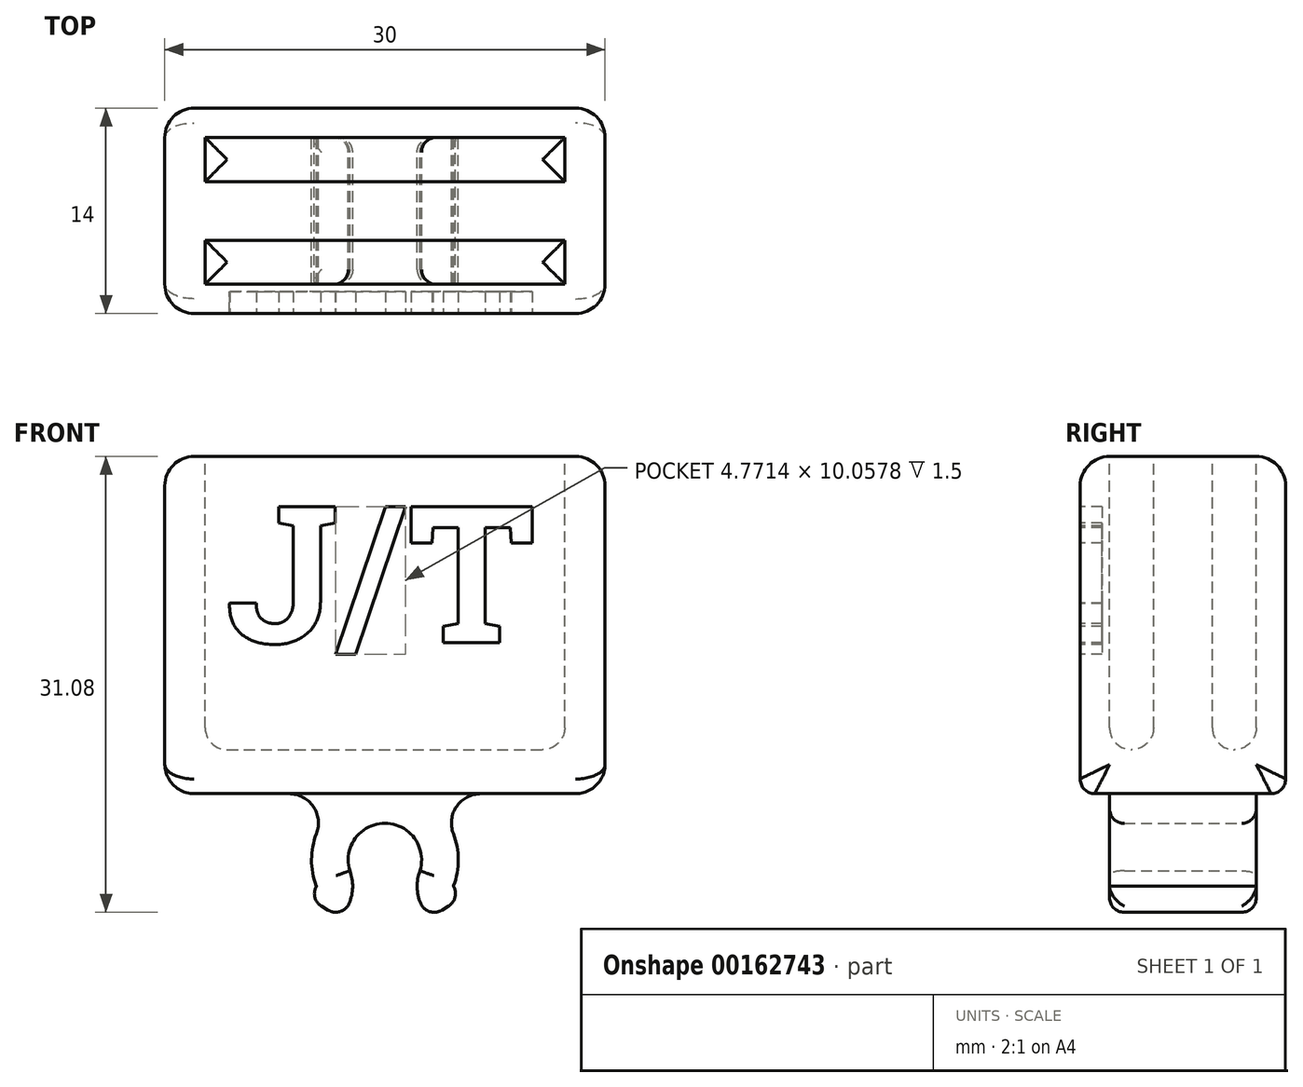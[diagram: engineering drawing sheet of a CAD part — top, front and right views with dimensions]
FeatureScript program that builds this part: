
annotation { "Feature Type Name" : "Feature", "Feature Type Description" : "" }
export const myFeature = defineFeature(function(context is Context, id is Id, definition is map)
    precondition{}
    {
        {
            var Q0;
            Q0=qCreatedBy(makeId("Front.planeOp"),FACE);
            var sketch = newSketch(context, id + "F0", { "sketchPlane" : qUnion([Q0])});
            skArc(sketch, "E0", {"start": v(2.39, -1.95) * mm, "mid": v(2.01, 0.27) * mm, "end": v(0, 1.28) * mm});
            skArc(sketch, "E1", {"start": v(2.39, -1.95) * mm, "mid": v(2.27, -3.64) * mm, "end": v(3.08, -5.12) * mm});
            skLineSegment(sketch, "E2", {"start": v(3.08, -5.12) * mm, "end": v(5.18, -3.84) * mm});
            skLineSegment(sketch, "E3", {"start": v(5.18, -3.84) * mm, "end": v(4.67, -3) * mm});
            skArc(sketch, "E4", {"start": v(4.67, -3) * mm, "mid": v(4.64, 0.64) * mm, "end": v(2.14, 3.3) * mm});
            skLineSegment(sketch, "E5", {"start": v(0, 8.47) * mm, "end": v(0, -7.46) * mm, "construction": true});
            skLineSegment(sketch, "E6", {"start": v(2.14, 3.3) * mm, "end": v(15, 3.3) * mm});
            skLineSegment(sketch, "E7", {"start": v(15, 3.3) * mm, "end": v(15, 26.3) * mm});
            skLineSegment(sketch, "E8", {"start": v(15, 26.3) * mm, "end": v(0, 26.3) * mm});
            skPoint(sketch, "E9.orphan", {"position": v(0, 3.78) * mm});
            skLineSegment(sketch, "E10.MirrorCS", {"start": v(-3.08, -5.12) * mm, "end": v(-5.18, -3.84) * mm});
            skLineSegment(sketch, "E11.MirrorCS", {"start": v(-5.18, -3.84) * mm, "end": v(-4.67, -3) * mm});
            skArc(sketch, "E12.MirrorCS", {"start": v(-2.39, -1.95) * mm, "mid": v(-2.27, -3.64) * mm, "end": v(-3.08, -5.12) * mm});
            skArc(sketch, "E13.MirrorCS", {"start": v(-2.39, -1.95) * mm, "mid": v(-2.01, 0.27) * mm, "end": v(0, 1.28) * mm});
            skLineSegment(sketch, "E14.MirrorCS", {"start": v(-15, 3.3) * mm, "end": v(-15, 26.3) * mm});
            skLineSegment(sketch, "E15.MirrorCS", {"start": v(-2.14, 3.3) * mm, "end": v(-15, 3.3) * mm});
            skLineSegment(sketch, "E16.MirrorCS", {"start": v(-15, 26.3) * mm, "end": v(0, 26.3) * mm});
            skArc(sketch, "E17.MirrorCS", {"start": v(-4.67, -3) * mm, "mid": v(-4.64, 0.64) * mm, "end": v(-2.14, 3.3) * mm});
            skSolve(sketch);
        }
        {
            var Q0;
            Q0=makeQuery(id+"F0.imprint","IMPRINT",FACE,{"disambiguationData":[TD([[makeQuery(id+"F0.imprint","IMPRINT",EDGE,{"derivedFrom":sQuery(id+"F0.wireOp",EDGE,"E0")}),-1.0]])]});
            extrude(context, id + "F1", {"entities" : qUnion([Q0]), "depth" : 10 * mm});
        }
        {
            var Q0;
            Q0=makeQuery(id+"F1.opExtrude","CAP_FACE",FACE,{"disambiguationData":[OSD([sQuery(id+"F0.wireOp",EDGE,"E0"),sQuery(id+"F0.wireOp",EDGE,"E1"),sQuery(id+"F0.wireOp",EDGE,"E2"),sQuery(id+"F0.wireOp",EDGE,"E3"),sQuery(id+"F0.wireOp",EDGE,"E4"),sQuery(id+"F0.wireOp",EDGE,"E6"),sQuery(id+"F0.wireOp",EDGE,"E7"),sQuery(id+"F0.wireOp",EDGE,"E8"),sQuery(id+"F0.wireOp",EDGE,"E10.MirrorCS"),sQuery(id+"F0.wireOp",EDGE,"E11.MirrorCS"),sQuery(id+"F0.wireOp",EDGE,"E12.MirrorCS"),sQuery(id+"F0.wireOp",EDGE,"E13.MirrorCS"),sQuery(id+"F0.wireOp",EDGE,"E14.MirrorCS"),sQuery(id+"F0.wireOp",EDGE,"E15.MirrorCS"),sQuery(id+"F0.wireOp",EDGE,"E16.MirrorCS"),sQuery(id+"F0.wireOp",EDGE,"E17.MirrorCS")])],"isStart":false});
            var sketch = newSketch(context, id + "F2", { "sketchPlane" : qUnion([Q0])});
            skLineSegment(sketch, "E18.bottom", {"start": v(-15, 3.3) * mm, "end": v(15, 3.3) * mm});
            skLineSegment(sketch, "E18.top", {"start": v(-15, 26.3) * mm, "end": v(15, 26.3) * mm});
            skLineSegment(sketch, "E18.left", {"start": v(-15, 3.3) * mm, "end": v(-15, 26.3) * mm});
            skLineSegment(sketch, "E18.right", {"start": v(15, 3.3) * mm, "end": v(15, 26.3) * mm});
            skSolve(sketch);
        }
        {
            var Q0;
            Q0 = qSketchRegion(id + "F2", true);
            extrude(context, id + "F3", {"entities" : qUnion([Q0]), "operationType" : NewBodyOperationType.ADD, "depth" : 2 * mm});
        }
        {
            var Q0;
            Q0=makeQuery(id+"F1.opExtrude","CAP_FACE",FACE,{"disambiguationData":[OSD([sQuery(id+"F0.wireOp",EDGE,"E0"),sQuery(id+"F0.wireOp",EDGE,"E1"),sQuery(id+"F0.wireOp",EDGE,"E2"),sQuery(id+"F0.wireOp",EDGE,"E3"),sQuery(id+"F0.wireOp",EDGE,"E4"),sQuery(id+"F0.wireOp",EDGE,"E6"),sQuery(id+"F0.wireOp",EDGE,"E7"),sQuery(id+"F0.wireOp",EDGE,"E8"),sQuery(id+"F0.wireOp",EDGE,"E10.MirrorCS"),sQuery(id+"F0.wireOp",EDGE,"E11.MirrorCS"),sQuery(id+"F0.wireOp",EDGE,"E12.MirrorCS"),sQuery(id+"F0.wireOp",EDGE,"E13.MirrorCS"),sQuery(id+"F0.wireOp",EDGE,"E14.MirrorCS"),sQuery(id+"F0.wireOp",EDGE,"E15.MirrorCS"),sQuery(id+"F0.wireOp",EDGE,"E16.MirrorCS"),sQuery(id+"F0.wireOp",EDGE,"E17.MirrorCS")])],"isStart":true});
            var sketch = newSketch(context, id + "F4", { "sketchPlane" : qUnion([Q0])});
            skLineSegment(sketch, "E19.bottom", {"start": v(-15, 3.3) * mm, "end": v(15, 3.3) * mm});
            skLineSegment(sketch, "E19.top", {"start": v(-15, 26.3) * mm, "end": v(15, 26.3) * mm});
            skLineSegment(sketch, "E19.left", {"start": v(-15, 3.3) * mm, "end": v(-15, 26.3) * mm});
            skLineSegment(sketch, "E19.right", {"start": v(15, 3.3) * mm, "end": v(15, 26.3) * mm});
            skSolve(sketch);
        }
        {
            var Q0;
            Q0 = qSketchRegion(id + "F4", true);
            extrude(context, id + "F5", {"entities" : qUnion([Q0]), "operationType" : NewBodyOperationType.ADD, "depth" : 2 * mm});
        }
        {
            var Q0;
            Q0=makeQuery(id+"F5.boolean.opBoolean","MERGE",FACE,{"derivedFrom":[makeQuery(id+"F3.boolean.opBoolean","MERGE",FACE,{"derivedFrom":[makeQuery(id+"F1.opExtrude","SWEPT_FACE",FACE,{"disambiguationData":[OSD([sQuery(id+"F0.wireOp",EDGE,"E8"),sQuery(id+"F0.wireOp",EDGE,"E16.MirrorCS")])]}),makeQuery(id+"F3.opExtrude","SWEPT_FACE",FACE,{"disambiguationData":[OSD([sQuery(id+"F2.wireOp",EDGE,"E18.top")])]})]}),makeQuery(id+"F5.opExtrude","SWEPT_FACE",FACE,{"disambiguationData":[OSD([sQuery(id+"F4.wireOp",EDGE,"E19.top")])]})]});
            var sketch = newSketch(context, id + "F6", { "sketchPlane" : qUnion([Q0])});
            skLineSegment(sketch, "E20.bottom", {"start": v(12.25, -10) * mm, "end": v(-12.25, -10) * mm});
            skLineSegment(sketch, "E20.top", {"start": v(12.25, -7) * mm, "end": v(-12.25, -7) * mm});
            skLineSegment(sketch, "E20.left", {"start": v(12.25, -10) * mm, "end": v(12.25, -7) * mm});
            skLineSegment(sketch, "E20.right", {"start": v(-12.25, -10) * mm, "end": v(-12.25, -7) * mm});
            skPoint(sketch, "E20.middle", {"position": v(0, -8.5) * mm});
            skLineSegment(sketch, "E21.bottom", {"start": v(12.25, -3) * mm, "end": v(-12.25, -3) * mm});
            skLineSegment(sketch, "E21.top", {"start": v(12.25, 0) * mm, "end": v(-12.25, 0) * mm});
            skLineSegment(sketch, "E21.left", {"start": v(12.25, -3) * mm, "end": v(12.25, 0) * mm});
            skLineSegment(sketch, "E21.right", {"start": v(-12.25, -3) * mm, "end": v(-12.25, 0) * mm});
            skPoint(sketch, "E21.middle", {"position": v(0, -1.5) * mm});
            skSolve(sketch);
        }
        {
            var Q0;
            Q0=makeQuery(id+"F6.imprint","IMPRINT",FACE,{"disambiguationData":[TD([[makeQuery(id+"F6.imprint","IMPRINT",EDGE,{"derivedFrom":sQuery(id+"F6.wireOp",EDGE,"E21.bottom")}),-1.0]])]});
            var Q1;
            Q1=makeQuery(id+"F6.imprint","IMPRINT",FACE,{"disambiguationData":[TD([[makeQuery(id+"F6.imprint","IMPRINT",EDGE,{"derivedFrom":sQuery(id+"F6.wireOp",EDGE,"E20.bottom")}),-1.0]])]});
            extrude(context, id + "F7", {"entities" : qUnion([Q0, Q1]), "operationType" : NewBodyOperationType.REMOVE, "oppositeDirection" : true, "depth" : 20 * mm});
        }
        {
            var Q0;
            Q0=makeQuery(id+"F3.opExtrude","CAP_FACE",FACE,{"disambiguationData":[OSD([sQuery(id+"F2.wireOp",EDGE,"E18.bottom"),sQuery(id+"F2.wireOp",EDGE,"E18.top"),sQuery(id+"F2.wireOp",EDGE,"E18.left"),sQuery(id+"F2.wireOp",EDGE,"E18.right")])],"isStart":false});
            var sketch = newSketch(context, id + "F8", { "sketchPlane" : qUnion([Q0])});
            skText(sketch, "E22", { "text": "J/T", "fontName": "RobotoSlab-Bold.ttf"});
            const initialGuessF8  = {"E22": [-0.01081, 0.01361, 1, 0, 0.00938]};
            skSetInitialGuess(sketch, initialGuessF8);
            skSolve(sketch);
        }
        {
            var Q0;
            Q0 = qSketchRegion(id + "F8", true);
            extrude(context, id + "F9", {"entities" : qUnion([Q0]), "operationType" : NewBodyOperationType.REMOVE, "oppositeDirection" : true, "depth" : 1.5 * mm});
        }
        {
            var Q0;
            Q0=makeQuery(id+"F1.opExtrude","SWEPT_FACE",FACE,{"disambiguationData":[OSD([sQuery(id+"F0.wireOp",EDGE,"E2")])]});
            var Q1;
            Q1=makeQuery(id+"F1.opExtrude","SWEPT_FACE",FACE,{"disambiguationData":[OSD([sQuery(id+"F0.wireOp",EDGE,"E10.MirrorCS")])]});
            var Q2;
            Q2=makeQuery(id+"F1.opExtrude","CAP_EDGE",EDGE,{"disambiguationData":[OSD([sQuery(id+"F0.wireOp",EDGE,"E1")])],"isStart":true});
            var Q3;
            Q3=makeQuery(id+"F1.opExtrude","CAP_EDGE",EDGE,{"disambiguationData":[OSD([sQuery(id+"F0.wireOp",EDGE,"E12.MirrorCS")])],"isStart":true});
            var Q4;
            Q4=makeQuery(id+"F1.opExtrude","CAP_EDGE",EDGE,{"disambiguationData":[OSD([sQuery(id+"F0.wireOp",EDGE,"E0"),sQuery(id+"F0.wireOp",EDGE,"E13.MirrorCS")])],"isStart":false});
            var Q5;
            Q5=makeQuery(id+"F1.opExtrude","CAP_EDGE",EDGE,{"disambiguationData":[OSD([sQuery(id+"F0.wireOp",EDGE,"E12.MirrorCS")])],"isStart":false});
            var Q6;
            Q6=makeQuery(id+"F1.opExtrude","CAP_EDGE",EDGE,{"disambiguationData":[OSD([sQuery(id+"F0.wireOp",EDGE,"E1")])],"isStart":false});
            fillet(context, id + "F10", {"entities" : qUnion([Q0, Q1, Q2, Q3, Q4, Q5, Q6]), "radius" : 1 * mm, "tangentPropagation" : true, "allowEdgeOverflow" : false});
        }
        {
            var Q0;
            Q0=makeQuery(id+"F1.opExtrude","SWEPT_EDGE",EDGE,{"disambiguationData":[OSD([sQuery(id+"F0.wireOp",EDGE,"E4"),sQuery(id+"F0.wireOp",EDGE,"E6")])]});
            var Q1;
            Q1=makeQuery(id+"F1.opExtrude","SWEPT_EDGE",EDGE,{"disambiguationData":[OSD([sQuery(id+"F0.wireOp",EDGE,"E15.MirrorCS"),sQuery(id+"F0.wireOp",EDGE,"E17.MirrorCS")])]});
            fillet(context, id + "F11", {"entities" : qUnion([Q0, Q1]), "radius" : 2 * mm, "tangentPropagation" : true, "allowEdgeOverflow" : false});
        }
        {
            var Q0;
            Q0=makeQuery(id+"F5.opExtrude","CAP_EDGE",EDGE,{"disambiguationData":[OSD([sQuery(id+"F4.wireOp",EDGE,"E19.left")])],"isStart":false});
            var Q1;
            Q1=makeQuery(id+"F5.opExtrude","CAP_EDGE",EDGE,{"disambiguationData":[OSD([sQuery(id+"F4.wireOp",EDGE,"E19.right")])],"isStart":false});
            var Q2;
            Q2=makeQuery(id+"F5.opExtrude","CAP_EDGE",EDGE,{"disambiguationData":[OSD([sQuery(id+"F4.wireOp",EDGE,"E19.top")])],"isStart":false});
            var Q3;
            Q3=makeQuery(id+"F5.boolean.opBoolean","MERGE",EDGE,{"derivedFrom":[makeQuery(id+"F3.boolean.opBoolean","MERGE",EDGE,{"derivedFrom":[makeQuery(id+"F1.opExtrude","SWEPT_EDGE",EDGE,{"disambiguationData":[OSD([sQuery(id+"F0.wireOp",EDGE,"E14.MirrorCS"),sQuery(id+"F0.wireOp",EDGE,"E16.MirrorCS")])]}),makeQuery(id+"F3.opExtrude","SWEPT_EDGE",EDGE,{"disambiguationData":[OSD([sQuery(id+"F2.wireOp",EDGE,"E18.top"),sQuery(id+"F2.wireOp",EDGE,"E18.left")])]})]}),makeQuery(id+"F5.opExtrude","SWEPT_EDGE",EDGE,{"disambiguationData":[OSD([sQuery(id+"F4.wireOp",EDGE,"E19.top"),sQuery(id+"F4.wireOp",EDGE,"E19.right")])]})]});
            var Q4;
            Q4=makeQuery(id+"F5.boolean.opBoolean","MERGE",FACE,{"derivedFrom":[makeQuery(id+"F3.boolean.opBoolean","MERGE",FACE,{"derivedFrom":[makeQuery(id+"F1.opExtrude","SWEPT_FACE",FACE,{"disambiguationData":[OSD([sQuery(id+"F0.wireOp",EDGE,"E14.MirrorCS")])]}),makeQuery(id+"F3.opExtrude","SWEPT_FACE",FACE,{"disambiguationData":[OSD([sQuery(id+"F2.wireOp",EDGE,"E18.left")])]})]}),makeQuery(id+"F5.opExtrude","SWEPT_FACE",FACE,{"disambiguationData":[OSD([sQuery(id+"F4.wireOp",EDGE,"E19.right")])]})]});
            var Q5;
            Q5=makeQuery(id+"F5.boolean.opBoolean","MERGE",FACE,{"derivedFrom":[makeQuery(id+"F3.boolean.opBoolean","MERGE",FACE,{"derivedFrom":[makeQuery(id+"F1.opExtrude","SWEPT_FACE",FACE,{"disambiguationData":[OSD([sQuery(id+"F0.wireOp",EDGE,"E7")])]}),makeQuery(id+"F3.opExtrude","SWEPT_FACE",FACE,{"disambiguationData":[OSD([sQuery(id+"F2.wireOp",EDGE,"E18.right")])]})]}),makeQuery(id+"F5.opExtrude","SWEPT_FACE",FACE,{"disambiguationData":[OSD([sQuery(id+"F4.wireOp",EDGE,"E19.left")])]})]});
            var Q6;
            Q6=makeQuery(id+"F3.opExtrude","CAP_EDGE",EDGE,{"disambiguationData":[OSD([sQuery(id+"F2.wireOp",EDGE,"E18.top")])],"isStart":false});
            fillet(context, id + "F12", {"entities" : qUnion([Q0, Q1, Q2, Q3, Q4, Q5, Q6]), "radius" : 2 * mm, "tangentPropagation" : true, "allowEdgeOverflow" : false});
        }
        {
            var Q0;
            Q0=makeQuery(id+"F3.opExtrude","CAP_EDGE",EDGE,{"disambiguationData":[OSD([sQuery(id+"F2.wireOp",EDGE,"E18.bottom")])],"isStart":true});
            var Q1;
            Q1=makeQuery(id+"F5.opExtrude","CAP_EDGE",EDGE,{"disambiguationData":[OSD([sQuery(id+"F4.wireOp",EDGE,"E19.bottom")])],"isStart":true});
            var Q2;
            Q2=makeQuery(id+"F5.opExtrude","CAP_EDGE",EDGE,{"disambiguationData":[OSD([sQuery(id+"F4.wireOp",EDGE,"E19.bottom")])],"isStart":false});
            var Q3;
            Q3=makeQuery(id+"F3.opExtrude","CAP_EDGE",EDGE,{"disambiguationData":[OSD([sQuery(id+"F2.wireOp",EDGE,"E18.bottom")])],"isStart":false});
            fillet(context, id + "F13", {"entities" : qUnion([Q0, Q1, Q2, Q3]), "radius" : 1 * mm, "tangentPropagation" : true, "allowEdgeOverflow" : false});
        }
        {
            var Q0;
            Q0=makeQuery(id+"F7.boolean.opBoolean","COPY",FACE,{"derivedFrom":makeQuery(id+"F7.opExtrude","CAP_FACE",FACE,{"disambiguationData":[OSD([sQuery(id+"F6.wireOp",EDGE,"E21.bottom"),sQuery(id+"F6.wireOp",EDGE,"E21.top"),sQuery(id+"F6.wireOp",EDGE,"E21.left"),sQuery(id+"F6.wireOp",EDGE,"E21.right")])],"isStart":false})});
            var Q1;
            Q1=makeQuery(id+"F7.boolean.opBoolean","COPY",FACE,{"derivedFrom":makeQuery(id+"F7.opExtrude","CAP_FACE",FACE,{"disambiguationData":[OSD([sQuery(id+"F6.wireOp",EDGE,"E20.bottom"),sQuery(id+"F6.wireOp",EDGE,"E20.top"),sQuery(id+"F6.wireOp",EDGE,"E20.left"),sQuery(id+"F6.wireOp",EDGE,"E20.right")])],"isStart":false})});
            fillet(context, id + "F14", {"entities" : qUnion([Q0, Q1]), "radius" : 1.5 * mm, "tangentPropagation" : true, "allowEdgeOverflow" : false});
        }
    });
